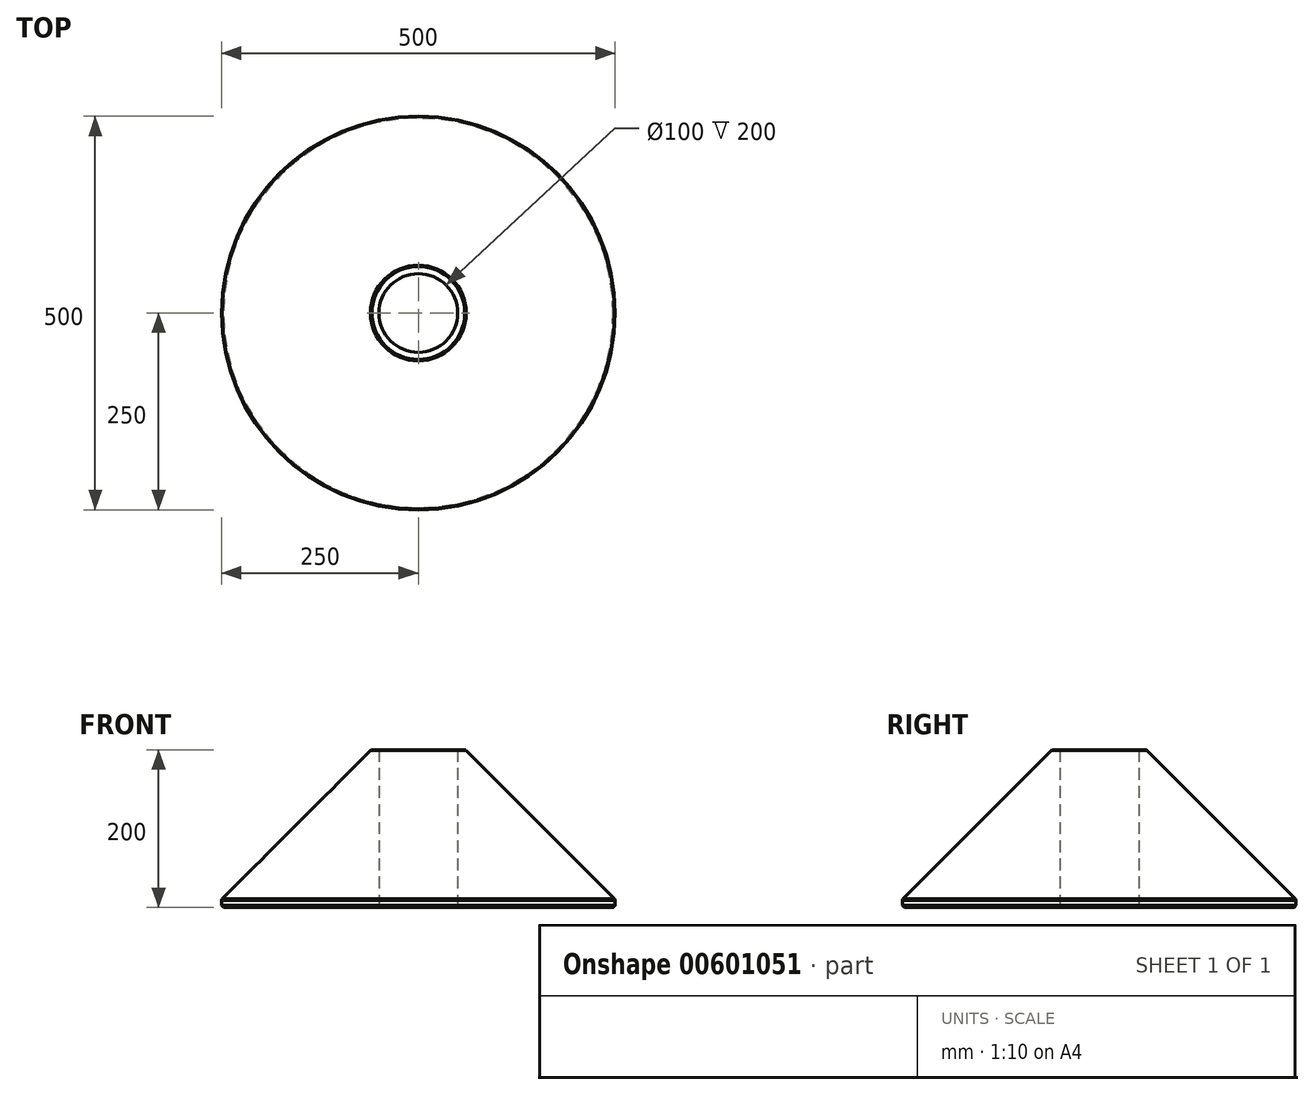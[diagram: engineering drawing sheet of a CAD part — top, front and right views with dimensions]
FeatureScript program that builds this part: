
annotation { "Feature Type Name" : "Feature", "Feature Type Description" : "" }
export const myFeature = defineFeature(function(context is Context, id is Id, definition is map)
    precondition{}
    {
        {
            var Q0;
            Q0=qCreatedBy(makeId("Top.planeOp"),FACE);
            var sketch = newSketch(context, id + "F0", { "sketchPlane" : qUnion([Q0])});
            skCircle(sketch, "E0", {"center": v(0, 0) * mm, "radius": 50 * mm});
            skCircle(sketch, "E1", {"center": v(0, 0) * mm, "radius": 250 * mm});
            skSolve(sketch);
        }
        {
            var Q0;
            Q0 = qSketchRegion(id + "F0", true);
            extrude(context, id + "F1", {"entities" : qUnion([Q0]), "depth" : 200 * mm, "offsetDistance" : 25 * mm});
        }
        {
            var Q0;
            Q0=makeQuery(id+"F1.opExtrude","CAP_EDGE",EDGE,{"disambiguationData":[OSD([sQuery(id+"F0.wireOp",EDGE,"E1")])],"isStart":false});
            chamfer(context, id + "F2", {"entities" : qUnion([Q0]), "width" : 190 * mm, "tangentPropagation" : true});
        }
        {
            var Q0;
            Q0=makeQuery(id+"F2.opChamfer","BLEND_FACE",FACE,{"disambiguationData":[OSD([sQuery(id+"F0.wireOp",EDGE,"E1")])]});
            var Q1;
            Q1=makeQuery(id+"F1.opExtrude","CAP_EDGE",EDGE,{"disambiguationData":[OSD([sQuery(id+"F0.wireOp",EDGE,"E1")])],"isStart":true});
            chamfer(context, id + "F3", {"entities" : qUnion([Q0, Q1]), "width" : 2.5 * mm, "tangentPropagation" : true});
        }
    });
